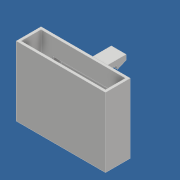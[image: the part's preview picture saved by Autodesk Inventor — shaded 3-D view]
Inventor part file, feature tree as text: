
AUTODESK INVENTOR PART (.ipt)
format: ipt  version: 2017 (Build 210142000, 142)  size: 204,800 bytes
history: native  units: mm
features: sketch x7, extrude x6, fillet x3, chamfer x2, hole x1, shell x1
ambient origin geometry x8: Origin, YZ Plane, XZ Plane, XY Plane, X Axis, Y Axis, Z Axis, Center Point
bodies: Solid1 (feature_tree)
feature tree (20):
  extrude  "Extrusion1"  Depth=33.02mm
  extrude  "Extrusion2"  Depth=4.0mm
  extrude  "Extrusion3"  Depth=12.0mm
  sketch  "Sketch4"  dims[d9=20.0mm d10=0.0mm d11=7.0mm]
  fillet  "Fillet1"  Radius=12.0mm
  hole  "Hole1"  [1 undecoded]
  extrude  "Extrusion4"  Depth=5.0mm
  extrude  "Extrusion5"  Depth=10.0mm
  chamfer  "Chamfer1"  Distance=3.0mm
  chamfer  "Chamfer2"  Distance=3.0mm
  fillet  "Fillet2"  Radius=7.0mm
  fillet  "Fillet3"  Radius=7.0mm
  extrude  "Extrusion6"  Depth=1.5mm
  shell  "Shell1"  Thickness=1.5mm
  sketch  "Sketch1"  dims[d0=52.07mm d1=33.02mm]
  sketch  "Sketch2"  dims[d2=7.0mm d3=0.0mm d4=4.0mm]
  sketch  "Sketch3"  dims[d5=4.0mm d6=0.0mm d7=12.0mm d8=12.0mm]
  sketch  "Sketch5"  dims[d12=1.5mm d13=5.0mm]
  sketch  "Sketch6"  dims[d14=10.0mm d15=10.0mm]
  sketch  "Sketch7"  dims[d16=5.0mm d17=3.0mm d18=5.984mm d19=10.0mm d20=2.0mm d21=120.0deg d22=10.688mm d23=20.594885mm d24=3.0mm d25=0.0mm d26=3.0mm d27=0.0mm d28=7.0mm d29=3.0mm d30=45.0deg d31=7.0mm d32=3.0mm d33=45.0deg d34=1.5mm d35=1.5mm d36=72.0mm d37=56.0mm d38=20.0mm d39=0.0mm d40=2.0mm]
note: 1 required parameter value undecoded (feature->parameter linkage not recoverable at this tier; creation-order binding heuristic only, values carry confidence <= 0.55)
